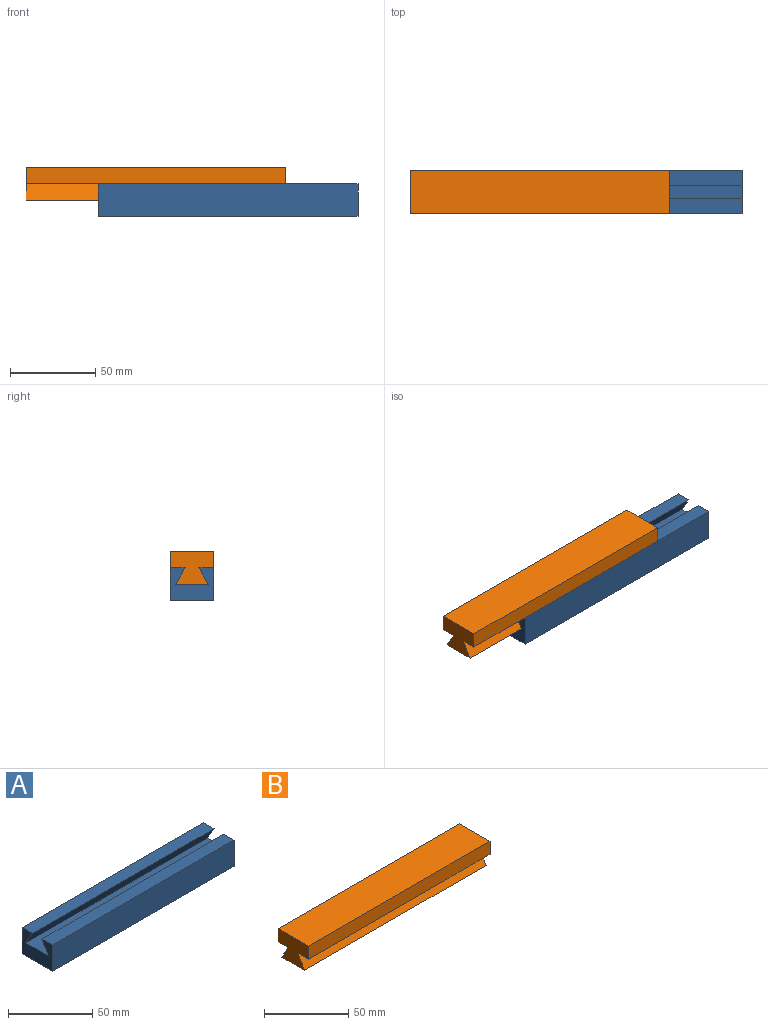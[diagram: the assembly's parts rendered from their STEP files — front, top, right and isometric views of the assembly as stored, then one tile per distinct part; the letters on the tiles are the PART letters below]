
ASSEMBLY  parts=2 mates=1
PART A: 10 faces, bbox 152.4x25.4x19.1 mm
  f0: plane 152.4x8.67mm, normal (0,0,1), area 1322mm2, adj f1,f2,f4,f8
  f1: plane 152.4x19.05mm, normal (0,1,0), area 2903.2mm2, adj f0,f2,f4,f6
  f2: plane 25.4x19.05mm, normal (-1,0,0), area 354.8mm2, adj f0,f1,f3,f5,f6,f7,f8,f9
  f3: plane 152.4x19.05mm, normal (0,-1,0), area 2903.2mm2, adj f2,f4,f5,f6
  f4: plane 25.4x19.05mm, normal (1,0,0), area 354.8mm2, adj f0,f1,f3,f5,f6,f7,f8,f9
  f5: plane 152.4x8.67mm, normal (0,0,1), area 1322mm2, adj f2,f3,f4,f7
  f6: plane 152.4x25.4mm, normal (0,0,-1), area 3871mm2, adj f1,f2,f3,f4
  f7: plane 152.4x9.53mm, normal (0,0.87,-0.5), area 1676.2mm2, adj f2,f4,f5,f9
  f8: plane 152.4x9.53mm, normal (0,-0.87,-0.5), area 1676.2mm2, adj f0,f2,f4,f9
  f9: plane 152.4x19.05mm, normal (0,0,1), area 2903.2mm2, adj f2,f4,f7,f8
PART B: 10 faces, bbox 152.4x25.4x19.1 mm
  f0: plane 25.4x19.05mm, normal (1,0,0), area 371mm2, adj f1,f3,f4,f5,f6,f7,f8,f9
  f1: plane 152.4x19.05mm, normal (0,0,-1), area 2903.2mm2, adj f0,f2,f6,f8
  f2: plane 25.4x19.05mm, normal (-1,0,0), area 371mm2, adj f1,f3,f4,f5,f6,f7,f8,f9
  f3: plane 152.4x9.53mm, normal (0,-1,0), area 1451.6mm2, adj f0,f2,f5,f9
  f4: plane 152.4x9.53mm, normal (0,1,0), area 1451.6mm2, adj f0,f2,f5,f7
  f5: plane 152.4x25.4mm, normal (0,0,1), area 3871mm2, adj f0,f2,f3,f4
  f6: plane 152.4x9.53mm, normal (0,0.87,0.5), area 1676.2mm2, adj f0,f1,f2,f7
  f7: plane 152.4x8.67mm, normal (0,0,-1), area 1322mm2, adj f0,f2,f4,f6
  f8: plane 152.4x9.53mm, normal (0,-0.87,0.5), area 1676.2mm2, adj f0,f1,f2,f9
  f9: plane 152.4x8.67mm, normal (0,0,-1), area 1322mm2, adj f0,f2,f3,f8
PLACE A t=(-4.01,33.39,-24.38)mm fixed
PLACE B t=(-47.3,74.78,-14.85)mm
MATE slider B.f2 <-> A.f2  axis (1,0,0) through (-69.36,27.32,-5.33)mm
